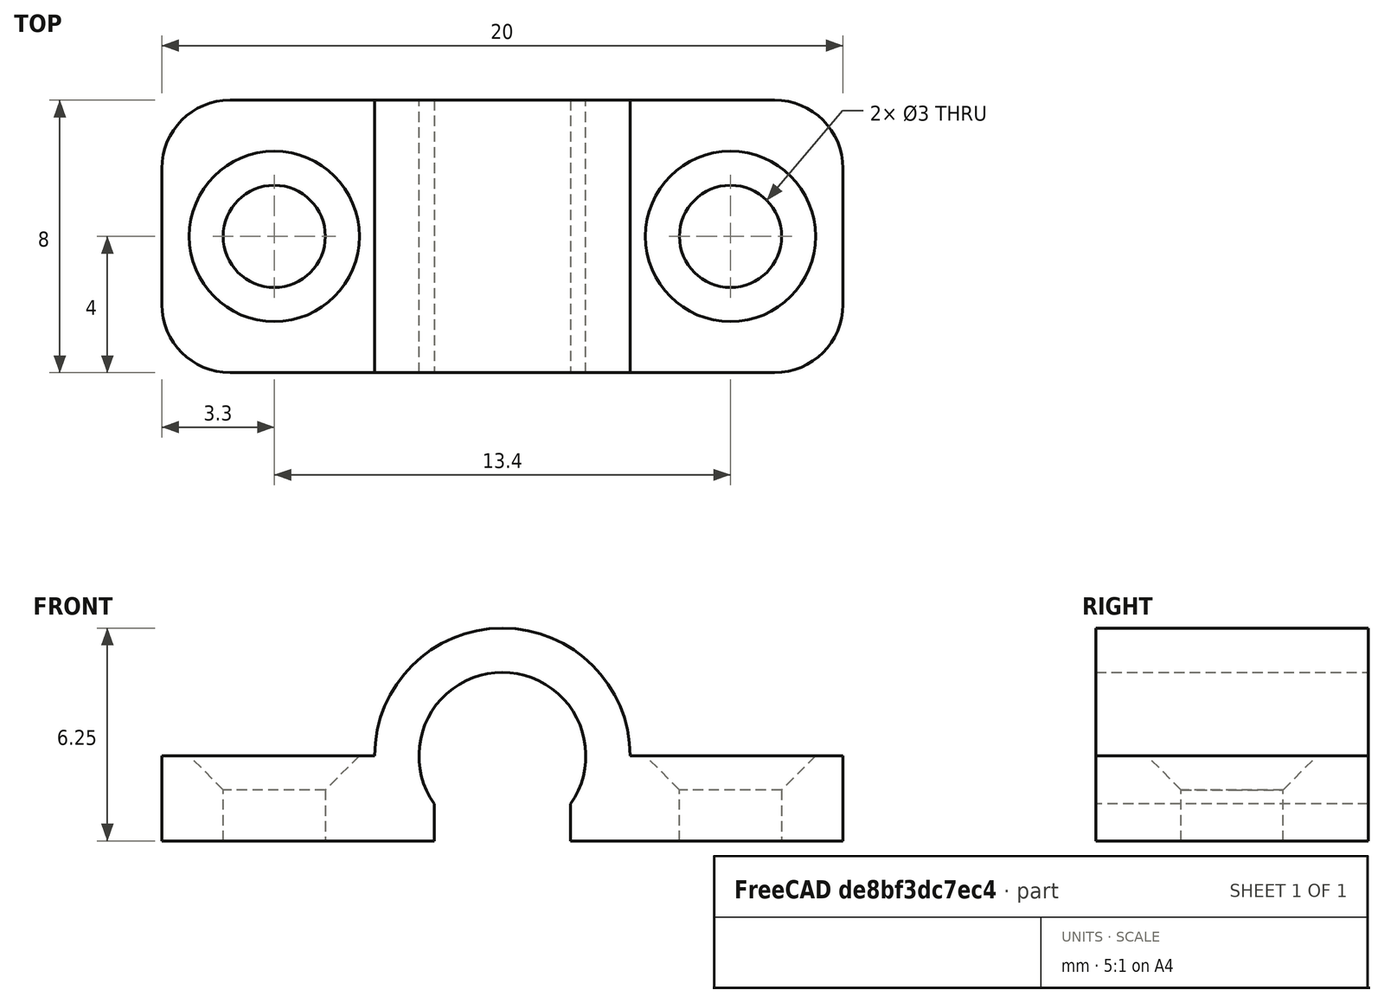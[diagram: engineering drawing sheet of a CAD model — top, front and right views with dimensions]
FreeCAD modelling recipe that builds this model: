
FCSTD DOCUMENT  (FreeCAD 0.21R32110 (Git))
Label: 3Cable_Clip_4_7mm
License: All rights reserved
LicenseURL: http://en.wikipedia.org/wiki/All_rights_reserved
objects: Sketcher::SketchObject×2, PartDesign::Pad×1, PartDesign::Body×1, App::Part×1
note: 5 computed .brp shape members not serialized (recipe doc carries the construction recipe); baked Part::Feature solids carry a one-line shape summary decoded from their .brp

FEATURE [Sketcher::SketchObject] Sketch
  FullyConstrained = false
  MapMode = 5
  Placement = pos=(0,0,0) rot=(1,0,0;1.5708rad)
  Support = -> [XZ_Plane001]
  sketch-geometry (14):
    g0: ArcOfCircle CenterX=9 CenterY=2.5 CenterZ=0 NormalX=0 NormalY=0 NormalZ=1 AngleXU=0 Radius=2.45 StartAngle=0.537843 EndAngle=3.59728
    g1: LineSegment StartX=0 StartY=0 StartZ=0 EndX=6.8 EndY=0 EndZ=0
    g2: LineSegment StartX=28 StartY=0 StartZ=0 EndX=28 EndY=2.5 EndZ=0
    g3: LineSegment StartX=0 StartY=2.5 StartZ=0 EndX=0 EndY=0 EndZ=0
    g4: LineSegment StartX=5.25 StartY=2.5 StartZ=0 EndX=0 EndY=2.5 EndZ=0
    g5: LineSegment StartX=6.8 StartY=1.42181 StartZ=0 EndX=6.8 EndY=0 EndZ=0
    g6: LineSegment StartX=21.2 StartY=0 StartZ=0 EndX=28 EndY=0 EndZ=0
    g7: ArcOfCircle CenterX=14 CenterY=2.5 CenterZ=0 NormalX=0 NormalY=0 NormalZ=1 AngleXU=0 Radius=2.45 StartAngle=0.537843 EndAngle=2.60375
    g8: LineSegment StartX=10 StartY=3.7551 StartZ=0 EndX=20 EndY=3.7551 EndZ=0
    g9: Circle CenterX=19 CenterY=2.5 CenterZ=0 NormalX=0 NormalY=0 NormalZ=1 AngleXU=0 Radius=2.45
    g10: ArcOfCircle CenterX=19 CenterY=2.5 CenterZ=0 NormalX=0 NormalY=0 NormalZ=1 AngleXU=0 Radius=3.75 StartAngle=0 EndAngle=2.30052
    g11: LineSegment StartX=28 StartY=2.5 StartZ=0 EndX=22.75 EndY=2.5 EndZ=0
    g12: ArcOfCircle CenterX=14 CenterY=2.5 CenterZ=0 NormalX=0 NormalY=0 NormalZ=1 AngleXU=0 Radius=3.75 StartAngle=0.841069 EndAngle=2.30052
    g13: ArcOfCircle CenterX=9 CenterY=2.5 CenterZ=0 NormalX=0 NormalY=0 NormalZ=1 AngleXU=0 Radius=3.75 StartAngle=0.841069 EndAngle=3.14159
  constraints (43):
    c: Diameter(g0) = 4.9
    c: Coincident(g6,g2)
    c: Coincident(g4,g3)
    c: Coincident(g3,g1)
    c: Horizontal(g1)
    c: Vertical(g2)
    c: Vertical(g3)
    c: Coincident(g1,g-1)
    c: Coincident(g4,g13)
    c: Vertical(g5)
    c: Coincident(g5,g0)
    c: Coincident(g5,g1)
    c: Distance(g3) = 2.5
    c: Equal(g3,g2)
    c: DistanceY(g0) = 2.5
    c: Horizontal(g6)
    c: Horizontal(g4)
    c: Horizontal(g8)
    c: Coincident(g10,g9)
    c: Equal(g0,g7)
    c: Equal(g7,g9)
    c: Coincident(g11,g2)
    c: Horizontal(g11)
    c: Coincident(g10,g11)
    c: DistanceX(g0) = 9
    c: Distance(g1) = 6.8
    c: Equal(g1,g6)
    c: PointOnObject(g7,g8)
    c: PointOnObject(g7,g8)
    c: PointOnObject(g0,g8)
    c: Coincident(g13,g12)
    c: Coincident(g10,g12)
    c: Equal(g4,g11)
    c: Distance(g4) = 5.25
    c: Equal(g13,g12)
    c: Equal(g12,g10)
    c: Horizontal(g1,g6)
    c: Coincident(g13,g0)
    c: Coincident(g12,g7)
    c: Horizontal(g0,g7)
    c: Horizontal(g7,g9)
    c: Distance(g0,g7) = 5
    c: Distance(g7,g9) = 5
FEATURE [PartDesign::Pad] Pad
  Direction = (0,-1,2e-16)
  Length = 8
  Length2 = 10
  Placement = pos=(0,0,0) rot=(1,0,0;1.5708rad)
  Profile = -> Sketch
  ReferenceAxis = -> Sketch [N_Axis]
  Type = 0
FEATURE [Sketcher::SketchObject] Sketch001
  AttachmentOffset = pos=(0,0,2.5) rot=(0,0,1;0rad)
  FullyConstrained = false
  MapMode = 5
  Placement = pos=(0,0,2.5) rot=(0,0,1;0rad)
  Support = -> [XY_Plane001]
  sketch-geometry (2):
    g0: Circle CenterX=3.3 CenterY=-4 CenterZ=0 NormalX=0 NormalY=0 NormalZ=1 AngleXU=0 Radius=1.5
    g1: Circle CenterX=16.7 CenterY=-4 CenterZ=0 NormalX=0 NormalY=0 NormalZ=1 AngleXU=0 Radius=1.5
  constraints (3):
    c: Equal(g0,g1)
    c: Diameter(g0) = 3
    c: DistanceY(g0) = -4
FEATURE [PartDesign::Body] Body
  Group = -> [Sketch,Pad,Sketch001]
  Origin = -> Origin001
  Tip = -> Pad
FEATURE [App::Part] Part
  Group = -> [Body]
  Origin = -> Origin
